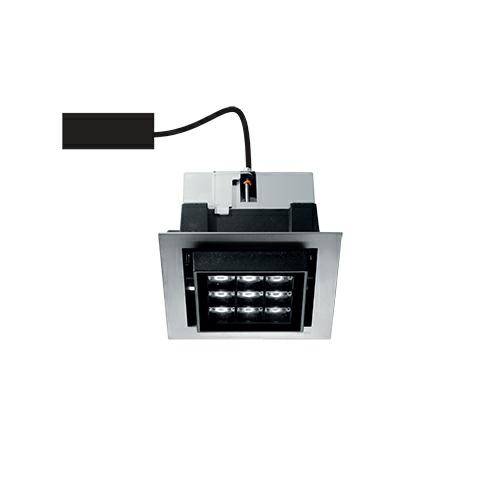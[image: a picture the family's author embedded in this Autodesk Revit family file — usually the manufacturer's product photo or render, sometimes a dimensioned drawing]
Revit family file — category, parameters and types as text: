
# Revit family: SIMES_S.7425W_Catch
name_source: partatom
category: Lighting Fixtures
revit_build: Autodesk Revit 2016 (Build: 20150714_1515(x64)
units: mm (PartAtom-declared; Revit-internal decimal feet)

## family parameters
Cut with Voids When Loaded = No
Host = Face
Light Source = Yes
OmniClass Number = 23.80.70.14
OmniClass Title = Luminaries for External Lighting
Part Type = Normal
Room Calculation Point = No
Round Connector Dimension = Use Diameter
Shared = No

## types (1)
- SIMES_S.7425W_Catch
    Approval mark = CE
    Assembly Code = D5020
    BIMobject category = Outside
    Brand url = http://www.simes.it
    Color Filter = 16777215
    Color Rendering Index = CRI 90
    Colour Temperature = 3000
    Control Gear = electronic transformer
    Default Elevation = 1219 mm
    Description = CATCH SQUARE 9LED
Art. S.7425W.19
MODULES LED 3000K  230V CRI 90
Rated luminaire luminous flux: 985lm
Rated input power: 15W
Luminaire efficacy: 66lm/W
Electronic ballast 220V240V 50/60Hz
CE

PRODUCT TYPE
False ceiling-recessed down-light fitting. IP rating IP 65
MATERIAL CHARACTERISTICS
Aluminium die cast housing in EN AB-47100 (low copper content) with high resistance against corrosion. Stone wash surface treatment prior to painting process. Aluminium front trim or Marine grade stainless steel AISI 316L front trim. A4 grade Stainless Steel screws with 2,5-3% molybdenum content which increases the resistance against corrosion. Pre treated Silicone Gaskets. Painting Process : 3 Step Process
1) Surface treatment with BONDERITE. A heavy metal free chemical surface treatment containing ceramic nano particles giving a cohesive, inorganic and highly dense protective coating. 2) PRE POLYMERIZATION a process of introducing an epoxy primer with excellent characteristics to the paint which also offers very high resistance to oxidation due to its Zinc content. 3) POLYMERIZATION a process with the application of polyester powder with high resistance against UV rays and harsh weather conditions. Resistance test protection for Marine applications for 1200h.  Mechanical resistance IK 08
LIGHTING PERFORMANCE
Toughened  transparent  glass 5mm thick. Lamp  adjustable ±20° position. LOR -- 
INSTALLATION AND MANTEINANCE
The luminaires are fixed to the falseceiling by a heavy-duty bracket system, adjustable from inside the luminaire. 
WIRING
Electronic circuit 220V/230V 50/60Hz in power supply box. Luminaire hard wired with 0.4m H05RN-F cable. Isolation: CLASS II . Available colours: Stainless steel (cod.19). Weight:  Kg Glow Wire test: --
Lamp included.
REGISTERED DESIGN
This luminaire contains built-in LED modules with energy class: A, A+, A++. In case of damage or malfunction please contact the manufacturer to receive additional instructions on how to replace and relative spare parts to order. The LED modules cannot be handled in the luminaire by the end user (Regulation UE 874/2012).
LED circuit boards are engineered accordingly to actual Lumen Maintenance regulation (LM80) and Technical Memorandum (TM21) where uniformity and quality of light is 50.000 hours referred to L70  B20 Ta 25°C.Lifecycle refers to LED circuit boards only, all others components of the luminaire are excluded.
    Design country = Italy
    Dimming Lamp Color Temperature Shift = <None>
    Edition number = 1
    Frequency = 50/60Hz
    IFC Classification = Light Fixture
    IK Rating = IK 08
    Installation instructions = http://www.simes.it
    Lamp = LED
    Lamp Light Flux = 1390
    Lamp Power = 24,299999237060547
    Lamp count = 1
    Last Update = 02/08/2018 10:01:37
    Lifetime = 50000 L70 B20 Ta 25°C
    Light Output Ratio = 100
    Luminous efficacy = 65,7
    Manufacturer = SIMES
    Manufacturer country = Italy
    Manufacturer name = Simes
    Masterformat 2014 Code = 26 56 00
    Masterformat 2014 Description = Exterior Lighting
    Material main = Aluminium
    Material secondary = Glass
    Model = S.7425W
    Mounting Place = Ceiling
    Mounting Type = Recessed
    NBS Reference Code = 49
    NBS Reference Description = Luminaries And Lamps
    Nominal height = 0
    Nominal width = 0
    OmniClass Code = 23-35 47 11
    OmniClass Description = Lighting Fixture
    Photometric Web File = S7420W.ies
    Product Group = recessed luminaire
    Product Guid = 284f1ae0-b9ad-458c-8829-59ff5cf93d3c
    Product Name = Catch
    Product SKU = CATCH
    Product certification = http://www.simes.it
    Product data url = https://bimobject.com
    Product url = http://www.simes.it
    Protection Class = Protection class II
    Protection Degree = IP 65
    QR code = http://bimobject.com
    System Light Flux = 985
    System Power = 15
    Technical description = http://www.simes.it
    Tilt Angle = -90.00°
    Type Comments = SIMES S.p.A. - All rights reserved
    Type Image = catch-quad-9LED-bas_19.jpg
    UNSPSC Code = 3911
    URL = http://www.simes.it
    Uniclass 1.4 Code = YJ73
    Uniclass 1.4 Description = Luminaries and lamps
    Uniclass 2.0 Code = PR-49
    Uniclass 2.0 Description = Luminaries and lamps
    Uniclass 2015 Code = EF_70_80
    Uniclass 2015 Name = Lighting
    Uniformat II Code = D5020
    Uniformat II Description = Lighting & Branch Wiring
    Voltage = 220V240V
    Wattage Comments = 27.0W
    Weight Net (Kg) = 0

## geometry (parser evidence)
native form markers: Blend x4
no freeform markers — native parametric forms only
